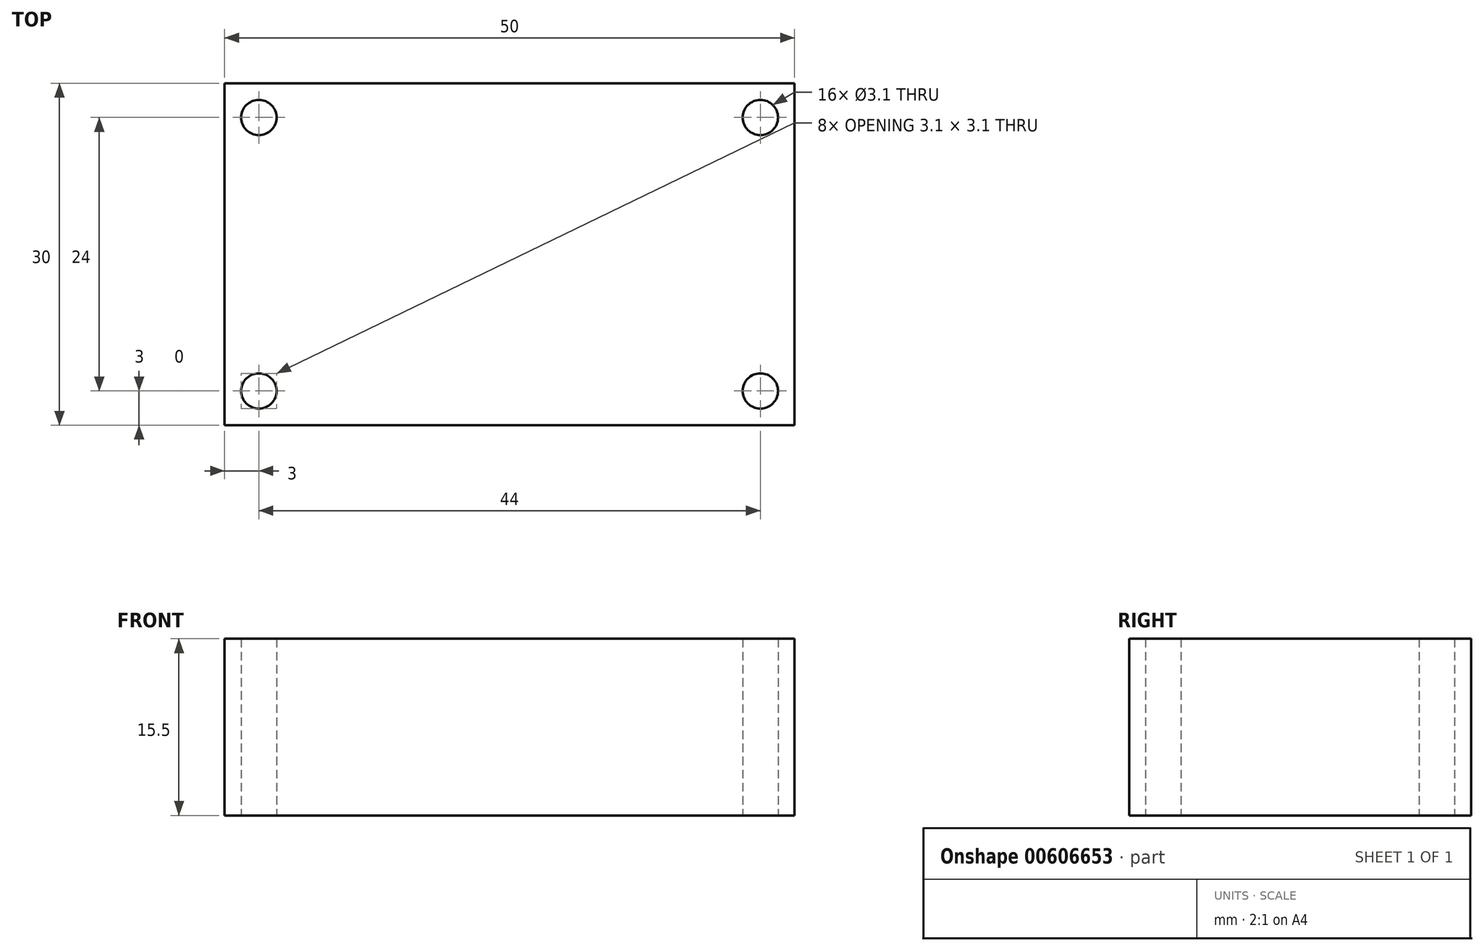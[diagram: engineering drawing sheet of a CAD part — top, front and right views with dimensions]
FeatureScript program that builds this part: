
annotation { "Feature Type Name" : "Feature", "Feature Type Description" : "" }
export const myFeature = defineFeature(function(context is Context, id is Id, definition is map)
    precondition{}
    {
        {
            var Q0;
            Q0=qCreatedBy(makeId("Top.planeOp"),FACE);
            var sketch = newSketch(context, id + "F0", { "sketchPlane" : qUnion([Q0])});
            skLineSegment(sketch, "E0.bottom", {"start": v(25, 15) * mm, "end": v(-25, 15) * mm});
            skLineSegment(sketch, "E0.top", {"start": v(25, -15) * mm, "end": v(-25, -15) * mm});
            skLineSegment(sketch, "E0.left", {"start": v(25, 15) * mm, "end": v(25, -15) * mm});
            skLineSegment(sketch, "E0.right", {"start": v(-25, 15) * mm, "end": v(-25, -15) * mm});
            skPoint(sketch, "E0.middle", {"position": v(0, 0) * mm});
            skPoint(sketch, "E1", {"position": v(-22, 12) * mm});
            skPoint(sketch, "E2", {"position": v(-22, -12) * mm});
            skPoint(sketch, "E3", {"position": v(22, -12) * mm});
            skPoint(sketch, "E4", {"position": v(22, 12) * mm});
            skSolve(sketch);
        }
        {
            var Q0;
            Q0=makeQuery(id+"F0.imprint","IMPRINT",FACE,{"disambiguationData":[TD([[makeQuery(id+"F0.imprint","IMPRINT",EDGE,{"derivedFrom":sQuery(id+"F0.wireOp",EDGE,"E0.bottom")}),1.0]])]});
            extrude(context, id + "F1", {"entities" : qUnion([Q0]), "depth" : 15.5 * mm, "offsetDistance" : 25 * mm});
        }
        {
            var Q0;
            Q0=sQuery(id+"F0.wireOp",VERTEX,"E1");
            var Q1;
            Q1=sQuery(id+"F0.wireOp",VERTEX,"E4");
            var Q2;
            Q2=sQuery(id+"F0.wireOp",VERTEX,"E3");
            var Q3;
            Q3=sQuery(id+"F0.wireOp",VERTEX,"E2");
            var Q4;
            Q4=makeQuery(id+"F1.opExtrude","SWEPT_BODY",BODY,{"disambiguationData":[OSD([sQuery(id+"F0.wireOp",EDGE,"E0.bottom"),sQuery(id+"F0.wireOp",EDGE,"E0.top"),sQuery(id+"F0.wireOp",EDGE,"E0.left"),sQuery(id+"F0.wireOp",EDGE,"E0.right")])]});
            hole(context, id + "F2", {"style" : HoleStyle.SIMPLE, "endStyle" : HoleEndStyle.THROUGH, "oppositeDirection" : true, "holeDiameter" : 3.1 * mm, "majorDiameter" : 5 * mm, "isTappedThrough" : true, "tappedDepth" : 3.5 * mm, "tapClearance" : 3, "locations" : qUnion([Q0, Q1, Q2, Q3]), "scope" : qUnion([Q4])});
        }
    });
